# Revit family: bfs-300ta2-60_60Hz
name_source: partatom
category: 機械設備
units: mm (PartAtom-declared; Revit-internal decimal feet)

## family parameters
OmniClass タイトル = Axial Fans
OmniClass 番号 = 23.75.35.17.24
パーツ タイプ = 割り込み
ロード時にボイドで切り取り = いいえ
丸型コネクタ寸法 = 直径を使用
作業面ベース = いいえ
共有 = いいえ
常に垂直 = はい
部屋計算ポイント = はい

## types (1)
- BFS-300TA2-60
    Clearance Back = 0  [stored 0 ft]
    Clearance Bottom = 0  [stored 0 ft]
    Clearance Front = 0  [stored 0 ft]
    Clearance Left = 450  [stored 1.47638 ft]
    Clearance Right = 0  [stored 0 ft]
    Clearance Top = 0  [stored 0 ft]
    Depth = 775  [stored 2.54265 ft]
    Height = 413  [stored 1.35499 ft]
    IfcExportAs = IfcFanType
    IfcExportType = CENTRIFUGALFORWARDCURVED
    M = 79
    MAX静圧 = 460.0 Pa
    MAX風量 = 3000.0 m³/h
    MID静圧 = 0.0 Pa
    MID風量 = 0.0 m³/h
    MIN静圧 = 0.0 Pa
    MIN風量 = 0.0 m³/h
    OmniClassCode = 23-33 31 19 13 15
    URL = https://www.mitsubishielectric.co.jp
    Uniclass2015Code = Pr_65_67_29_12
    Uniclass2015Title = Centrifugal fans
    Uniclass2015Version = Systems v1.9
    Width = 586  [stored 1.92257 ft]
    サービススペース = はい
    ダクト幅 = 300 mm
    ダクト高 = 300 mm
    ファンの種類 = 多翼形
    モデル = BFS-300TA2-60
    仕様書バージョン = Version1.0
    企業コード = 108420
    価格 = 266000 $
    分類コード = 50052502100020
    周波数 = 60 Hz
    呼称 = 消音ボックス付送風機
    天吊金具ピッチ奥行 = 722  [stored 2.36877 ft]
    天吊金具ピッチ幅 = 695  [stored 2.28018 ft]
    実風量 = 0.0 m³/h
    形名 = BFS-TA : BFS-300TA
    本体マテリアル = 溶融亜鉛めっき鋼板
    極 = 4
    極数 = 3
    法定耐用年数 = 15
    消費電力 = 1270 W
    番手 = #2
    盤工事区分 = 電気工事
    相 = 3
    積算_科目 = 2 換気設備
    製品リリース年月 = 2022年6月1日
    製品出荷対象 = 国内
    製品質量 = 39.00 kg
    製造元 = 三菱電機株式会社
    設置方法 = 天吊
    説明 = ストレートシロッコファン天吊埋込タイプ（標準形）
    負荷分類 = 3_ファン類
    質量 = 46.80 kg
    運転質量 = 0.00 kg
    電動機出力 = 1500 W
    電圧 = 200 V
    騒音レベル(dB(A)) = 73
    騒音レベル(dB(A))_側面 = 46
    騒音レベル(dB(A))_吐出 = 73
    騒音レベル(dB(A))_吸込 = 56

note: [stored X ft] marks values corroborated as IEEE doubles in the binary element streams (Revit-internal decimal feet)
